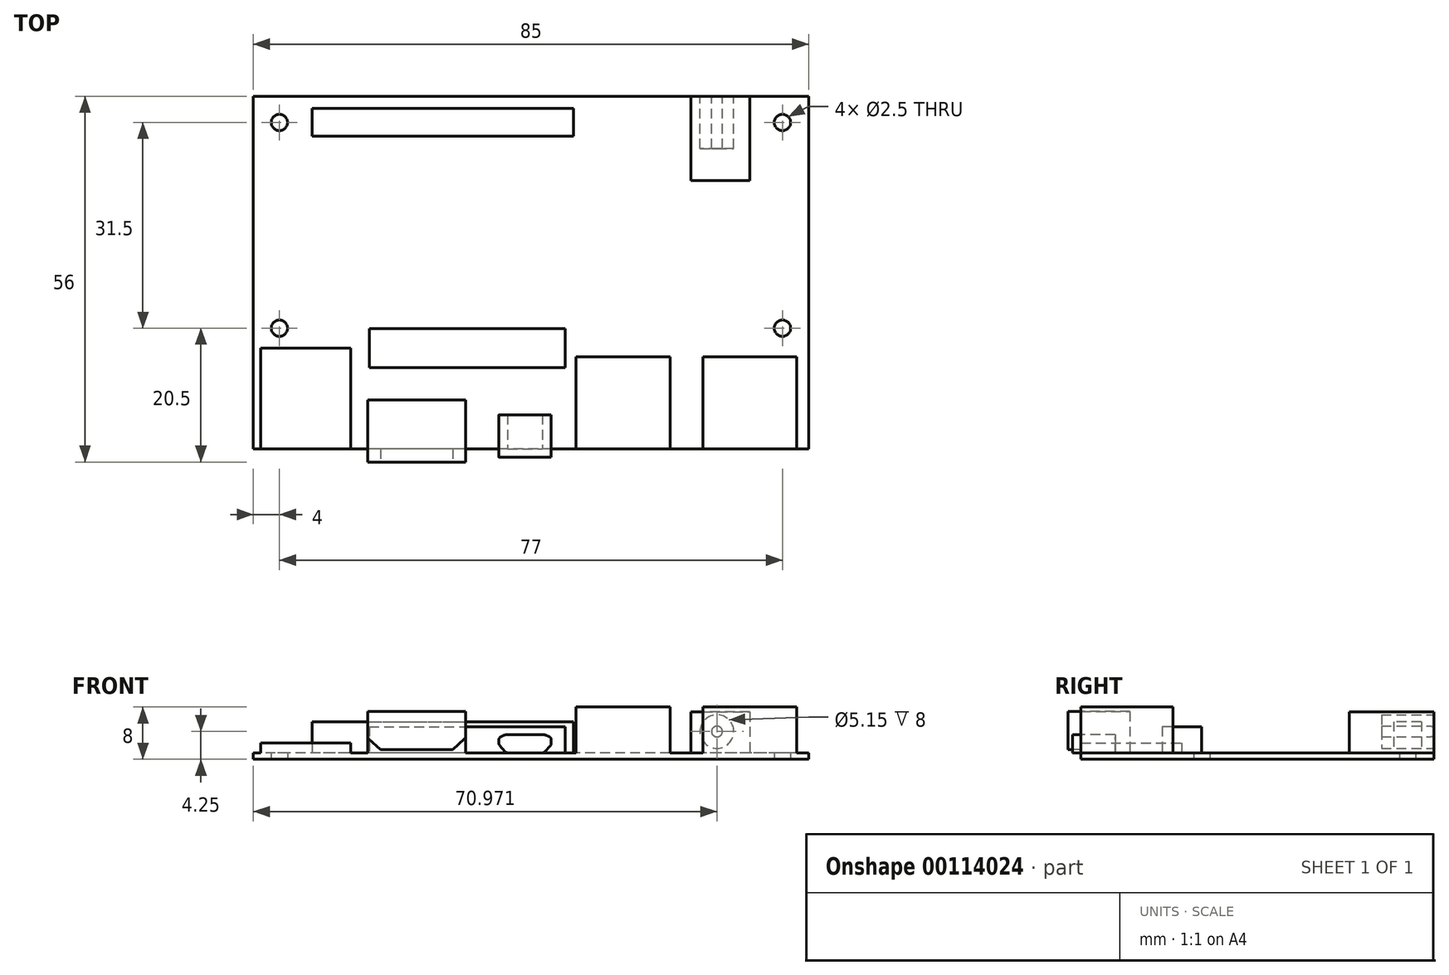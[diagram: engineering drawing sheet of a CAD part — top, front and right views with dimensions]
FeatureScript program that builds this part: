
annotation { "Feature Type Name" : "Feature", "Feature Type Description" : "" }
export const myFeature = defineFeature(function(context is Context, id is Id, definition is map)
    precondition{}
    {
        {
            var Q0;
            Q0=qCreatedBy(makeId("Top.planeOp"),FACE);
            var sketch = newSketch(context, id + "F0", { "sketchPlane" : qUnion([Q0])});
            skLineSegment(sketch, "E0.bottom", {"start": v(42.5, -27) * mm, "end": v(-42.5, -27) * mm});
            skLineSegment(sketch, "E0.top", {"start": v(42.5, 27) * mm, "end": v(-42.5, 27) * mm});
            skLineSegment(sketch, "E0.left", {"start": v(42.5, -27) * mm, "end": v(42.5, 27) * mm});
            skLineSegment(sketch, "E0.right", {"start": v(-42.5, -27) * mm, "end": v(-42.5, 27) * mm});
            skPoint(sketch, "E0.middle", {"position": v(0, 0) * mm});
            skLineSegment(sketch, "E1", {"start": v(-38.5, 27) * mm, "end": v(-38.5, -27) * mm, "construction": true});
            skLineSegment(sketch, "E2", {"start": v(38.5, 27) * mm, "end": v(38.5, -27) * mm, "construction": true});
            skLineSegment(sketch, "E3", {"start": v(-42.5, 23) * mm, "end": v(42.5, 23) * mm, "construction": true});
            skLineSegment(sketch, "E4", {"start": v(-42.5, -8.5) * mm, "end": v(42.5, -8.5) * mm, "construction": true});
            skPoint(sketch, "E5", {"position": v(-38.5, 23) * mm});
            skPoint(sketch, "E6", {"position": v(38.5, 23) * mm});
            skPoint(sketch, "E7", {"position": v(38.5, -8.5) * mm});
            skPoint(sketch, "E8", {"position": v(-38.5, -8.5) * mm});
            skCircle(sketch, "E9", {"center": v(-38.5, 23) * mm, "radius": 1.25 * mm});
            skCircle(sketch, "E10", {"center": v(38.5, 23) * mm, "radius": 1.25 * mm});
            skCircle(sketch, "E11", {"center": v(38.5, -8.5) * mm, "radius": 1.25 * mm});
            skCircle(sketch, "E12", {"center": v(-38.5, -8.5) * mm, "radius": 1.25 * mm});
            skSolve(sketch);
        }
        {
            var Q0;
            Q0=makeQuery(id+"F0.imprint","IMPRINT",FACE,{"disambiguationData":[TD([[makeQuery(id+"F0.imprint","IMPRINT",EDGE,{"derivedFrom":sQuery(id+"F0.wireOp",EDGE,"E0.bottom")}),-1.0]])]});
            var sketch = newSketch(context, id + "F1", { "sketchPlane" : qUnion([Q0])});
            skLineSegment(sketch, "E13.bottom", {"start": v(-35, 26.25) * mm, "end": v(8, 26.25) * mm, "construction": true});
            skLineSegment(sketch, "E13.top", {"start": v(-35, 19.75) * mm, "end": v(8, 19.75) * mm, "construction": true});
            skLineSegment(sketch, "E13.left", {"start": v(-35, 26.25) * mm, "end": v(-35, 19.75) * mm, "construction": true});
            skLineSegment(sketch, "E13.right", {"start": v(8, 26.25) * mm, "end": v(8, 19.75) * mm, "construction": true});
            skPoint(sketch, "E14", {"position": v(-35, 23) * mm});
            skLineSegment(sketch, "E15", {"start": v(-32.5, 26.25) * mm, "end": v(-32.5, 19.75) * mm, "construction": true});
            skPoint(sketch, "E16", {"position": v(-32.53, 23) * mm});
            skLineSegment(sketch, "E17.bottom", {"start": v(-33.5, 25.12) * mm, "end": v(6.5, 25.12) * mm});
            skLineSegment(sketch, "E17.top", {"start": v(-33.5, 20.88) * mm, "end": v(6.5, 20.88) * mm});
            skLineSegment(sketch, "E17.left", {"start": v(-33.5, 25.12) * mm, "end": v(-33.5, 20.87) * mm});
            skLineSegment(sketch, "E17.right", {"start": v(6.5, 25.12) * mm, "end": v(6.5, 20.87) * mm});
            skSolve(sketch);
        }
        {
            var Q0;
            Q0=makeQuery(id+"F0.imprint","IMPRINT",FACE,{"disambiguationData":[TD([[makeQuery(id+"F0.imprint","IMPRINT",EDGE,{"derivedFrom":sQuery(id+"F0.wireOp",EDGE,"E0.bottom")}),-1.0]])]});
            var sketch = newSketch(context, id + "F2", { "sketchPlane" : qUnion([Q0])});
            skLineSegment(sketch, "E18.0", {"start": v(42.5, 27) * mm, "end": v(-42.5, 27) * mm});
            skLineSegment(sketch, "E19", {"start": v(24.5, 27) * mm, "end": v(24.5, 14.1) * mm});
            skLineSegment(sketch, "E20", {"start": v(24.5, 14.1) * mm, "end": v(33.5, 14.1) * mm});
            skLineSegment(sketch, "E21", {"start": v(33.5, 14.1) * mm, "end": v(33.5, 27) * mm});
            skLineSegment(sketch, "E22", {"start": v(29, 14.1) * mm, "end": v(29, 27) * mm, "construction": true});
            skLineSegment(sketch, "E23.0", {"start": v(-42.5, -27) * mm, "end": v(-42.5, 27) * mm});
            skSolve(sketch);
        }
        {
            var Q0;
            Q0=makeQuery(id+"F0.imprint","IMPRINT",FACE,{"disambiguationData":[TD([[makeQuery(id+"F0.imprint","IMPRINT",EDGE,{"derivedFrom":sQuery(id+"F0.wireOp",EDGE,"E0.bottom")}),-1.0]])]});
            var sketch = newSketch(context, id + "F3", { "sketchPlane" : qUnion([Q0])});
            skLineSegment(sketch, "E24.0", {"start": v(-42.5, -27) * mm, "end": v(-42.5, 27) * mm});
            skLineSegment(sketch, "E25.0", {"start": v(42.5, -27) * mm, "end": v(42.5, 27) * mm});
            skLineSegment(sketch, "E26", {"start": v(-42.5, -11.55) * mm, "end": v(42.5, -11.55) * mm, "construction": true});
            skLineSegment(sketch, "E27.0", {"start": v(42.5, -27) * mm, "end": v(-42.5, -27) * mm});
            skLineSegment(sketch, "E28", {"start": v(-34.5, -27) * mm, "end": v(-34.5, -11.55) * mm, "construction": true});
            skLineSegment(sketch, "E29", {"start": v(-17.5, -27) * mm, "end": v(-17.5, -11.55) * mm, "construction": true});
            skLineSegment(sketch, "E30", {"start": v(-25, -27) * mm, "end": v(-25, -19.5) * mm});
            skLineSegment(sketch, "E31", {"start": v(-25, -19.5) * mm, "end": v(-10, -19.5) * mm});
            skLineSegment(sketch, "E32", {"start": v(-10, -19.5) * mm, "end": v(-10, -27) * mm});
            skLineSegment(sketch, "E33", {"start": v(-41.38, -27) * mm, "end": v(-41.39, -11.55) * mm});
            skLineSegment(sketch, "E34", {"start": v(-41.39, -11.55) * mm, "end": v(-27.62, -11.55) * mm});
            skLineSegment(sketch, "E35", {"start": v(-27.62, -11.55) * mm, "end": v(-27.62, -27) * mm});
            skLineSegment(sketch, "E36", {"start": v(-0.9, -11.55) * mm, "end": v(-0.9, -27) * mm, "construction": true});
            skLineSegment(sketch, "E37", {"start": v(-4.9, -27) * mm, "end": v(-4.9, -21.75) * mm});
            skLineSegment(sketch, "E38", {"start": v(-4.9, -21.75) * mm, "end": v(3.1, -21.75) * mm});
            skLineSegment(sketch, "E39", {"start": v(3.1, -21.75) * mm, "end": v(3.1, -27) * mm});
            skLineSegment(sketch, "E40", {"start": v(14.1, -27) * mm, "end": v(14.1, -11.55) * mm, "construction": true});
            skLineSegment(sketch, "E41", {"start": v(33.5, -27) * mm, "end": v(33.5, -11.55) * mm, "construction": true});
            skLineSegment(sketch, "E42", {"start": v(6.9, -27) * mm, "end": v(6.9, -12.9) * mm});
            skLineSegment(sketch, "E43", {"start": v(6.9, -12.9) * mm, "end": v(21.3, -12.9) * mm});
            skLineSegment(sketch, "E44", {"start": v(21.3, -12.9) * mm, "end": v(21.3, -27) * mm});
            skLineSegment(sketch, "E45", {"start": v(26.3, -27) * mm, "end": v(26.3, -12.9) * mm});
            skLineSegment(sketch, "E46", {"start": v(26.3, -12.9) * mm, "end": v(40.7, -12.9) * mm});
            skLineSegment(sketch, "E47", {"start": v(40.7, -12.9) * mm, "end": v(40.7, -27) * mm});
            skLineSegment(sketch, "E48", {"start": v(-25, -27) * mm, "end": v(-25, -29) * mm});
            skLineSegment(sketch, "E49", {"start": v(-25, -29) * mm, "end": v(-10, -29) * mm});
            skLineSegment(sketch, "E50", {"start": v(-10, -29) * mm, "end": v(-10, -27) * mm});
            skLineSegment(sketch, "E51", {"start": v(-4.9, -27) * mm, "end": v(-4.9, -28.25) * mm});
            skLineSegment(sketch, "E52", {"start": v(-4.9, -28.25) * mm, "end": v(3.1, -28.25) * mm});
            skLineSegment(sketch, "E53", {"start": v(3.1, -28.25) * mm, "end": v(3.1, -27) * mm});
            skSolve(sketch);
        }
        {
            var Q0;
            Q0=makeQuery(id+"F0.imprint","IMPRINT",FACE,{"disambiguationData":[TD([[makeQuery(id+"F0.imprint","IMPRINT",EDGE,{"derivedFrom":sQuery(id+"F0.wireOp",EDGE,"E0.bottom")}),-1.0]])]});
            var sketch = newSketch(context, id + "F4", { "sketchPlane" : qUnion([Q0])});
            skLineSegment(sketch, "E54.bottom", {"start": v(-24.76, -8.55) * mm, "end": v(5.24, -8.55) * mm});
            skLineSegment(sketch, "E54.top", {"start": v(-24.76, -14.55) * mm, "end": v(5.24, -14.55) * mm});
            skLineSegment(sketch, "E54.left", {"start": v(-24.76, -8.55) * mm, "end": v(-24.76, -14.55) * mm});
            skLineSegment(sketch, "E54.right", {"start": v(5.24, -8.55) * mm, "end": v(5.24, -14.55) * mm});
            skLineSegment(sketch, "E55.0", {"start": v(-21.35, -27) * mm, "end": v(-21.35, -11.55) * mm});
            skLineSegment(sketch, "E55.1", {"start": v(-42.5, -27) * mm, "end": v(-42.5, 27) * mm});
            skSolve(sketch);
        }
        {
            var Q0;
            Q0=qSketchRegion(id+"F0",true);
            extrude(context, id + "F5", {"entities" : qUnion([Q0]), "depth" : 1 * mm});
        }
        {
            var Q0;
            {var subQ0=sQuery(id+"F3.wireOp",EDGE,"E45");Q0=makeQuery(id+"F3.imprint","IMPRINT",FACE,{"disambiguationData":[TD([[makeQuery(id+"F3.imprint","IMPRINT",EDGE,{"derivedFrom":subQ0}),-1.0]])]});}
            var Q1;
            {var subQ0=sQuery(id+"F3.wireOp",EDGE,"E42");Q1=makeQuery(id+"F3.imprint","IMPRINT",FACE,{"disambiguationData":[TD([[makeQuery(id+"F3.imprint","IMPRINT",EDGE,{"derivedFrom":subQ0}),-1.0]])]});}
            extrude(context, id + "F6", {"entities" : qUnion([Q0, Q1]), "operationType" : NewBodyOperationType.ADD, "depth" : 8 * mm});
        }
        {
            var Q0;
            {var subQ0=sQuery(id+"F3.wireOp",EDGE,"E51");Q0=makeQuery(id+"F3.imprint","IMPRINT",FACE,{"disambiguationData":[TD([[makeQuery(id+"F3.imprint","IMPRINT",EDGE,{"derivedFrom":subQ0}),1.0]])]});}
            var Q1;
            {var subQ0=sQuery(id+"F3.wireOp",EDGE,"E37");Q1=makeQuery(id+"F3.imprint","IMPRINT",FACE,{"disambiguationData":[TD([[makeQuery(id+"F3.imprint","IMPRINT",EDGE,{"derivedFrom":subQ0}),-1.0]])]});}
            extrude(context, id + "F7", {"entities" : qUnion([Q0, Q1]), "operationType" : NewBodyOperationType.ADD, "depth" : 3.75 * mm});
        }
        {
            var Q0;
            {var subQ0=sQuery(id+"F3.wireOp",EDGE,"E48");Q0=makeQuery(id+"F3.imprint","IMPRINT",FACE,{"disambiguationData":[TD([[makeQuery(id+"F3.imprint","IMPRINT",EDGE,{"derivedFrom":subQ0}),1.0]])]});}
            var Q1;
            {var subQ0=sQuery(id+"F3.wireOp",EDGE,"E30");Q1=makeQuery(id+"F3.imprint","IMPRINT",FACE,{"disambiguationData":[TD([[makeQuery(id+"F3.imprint","IMPRINT",EDGE,{"derivedFrom":subQ0}),-1.0]])]});}
            extrude(context, id + "F8", {"entities" : qUnion([Q0, Q1]), "operationType" : NewBodyOperationType.ADD, "depth" : 7.3 * mm});
        }
        {
            var Q0;
            {var subQ0=sQuery(id+"F3.wireOp",EDGE,"E33");Q0=makeQuery(id+"F3.imprint","IMPRINT",FACE,{"disambiguationData":[TD([[makeQuery(id+"F3.imprint","IMPRINT",EDGE,{"derivedFrom":subQ0}),-1.0]])]});}
            extrude(context, id + "F9", {"entities" : qUnion([Q0]), "operationType" : NewBodyOperationType.ADD, "depth" : 2.5 * mm});
        }
        {
            var Q0;
            {var subQ0=sQuery(id+"F2.wireOp",EDGE,"E19");Q0=makeQuery(id+"F2.imprint","IMPRINT",FACE,{"disambiguationData":[TD([[makeQuery(id+"F2.imprint","IMPRINT",EDGE,{"derivedFrom":subQ0}),1.0]])]});}
            extrude(context, id + "F10", {"entities" : qUnion([Q0]), "operationType" : NewBodyOperationType.ADD, "depth" : 7.25 * mm});
        }
        {
            var Q0;
            Q0=qSketchRegion(id+"F1",true);
            extrude(context, id + "F11", {"entities" : qUnion([Q0]), "operationType" : NewBodyOperationType.ADD, "depth" : 5.75 * mm});
        }
        {
            var Q0;
            Q0=qSketchRegion(id+"F4",true);
            extrude(context, id + "F12", {"entities" : qUnion([Q0]), "operationType" : NewBodyOperationType.ADD, "depth" : 5 * mm});
        }
        {
            var Q0;
            Q0=makeQuery(id+"F7.opExtrude","SWEPT_FACE",FACE,{"disambiguationData":[OSD([sQuery(id+"F3.wireOp",EDGE,"E52")])]});
            var sketch = newSketch(context, id + "F13", { "sketchPlane" : qUnion([Q0])});
            skPoint(sketch, "E56", {"position": v(-0.9, 0) * mm});
            skLineSegment(sketch, "E57", {"start": v(-4.9, 0) * mm, "end": v(-0.9, 0) * mm, "construction": true});
            skPoint(sketch, "E58", {"position": v(-2.9, 0) * mm});
            skLineSegment(sketch, "E59", {"start": v(-0.9, 0) * mm, "end": v(3.1, 0) * mm, "construction": true});
            skPoint(sketch, "E60", {"position": v(1.1, 0) * mm});
            skLineSegment(sketch, "E61", {"start": v(-4.77, 2.1) * mm, "end": v(-3.94, 1.17) * mm});
            skLineSegment(sketch, "E62", {"start": v(2.15, 1.17) * mm, "end": v(2.97, 2.08) * mm});
            skPoint(sketch, "E63", {"position": v(-3.94, 3.75) * mm});
            skPoint(sketch, "E64", {"position": v(2.14, 3.75) * mm});
            skLineSegment(sketch, "E65", {"start": v(-0.9, 0) * mm, "end": v(-0.9, 3.75) * mm, "construction": true});
            skLineSegment(sketch, "E66", {"start": v(-4.6, 3.48) * mm, "end": v(-4.08, 3.7) * mm});
            skLineSegment(sketch, "E67", {"start": v(2.8, 3.46) * mm, "end": v(2.28, 3.69) * mm});
            skLineSegment(sketch, "E68", {"start": v(-4.9, 2.24) * mm, "end": v(3.1, 2.22) * mm, "construction": true});
            skLineSegment(sketch, "E69", {"start": v(-4.9, 3.35) * mm, "end": v(3.1, 3.33) * mm, "construction": true});
            skLineSegment(sketch, "E70", {"start": v(-4.9, 3.02) * mm, "end": v(-4.9, 2.43) * mm});
            skLineSegment(sketch, "E71", {"start": v(3.1, 3) * mm, "end": v(3.1, 2.42) * mm});
            skLineSegment(sketch, "E72", {"start": v(-3.8, 3.75) * mm, "end": v(2, 3.75) * mm});
            skLineSegment(sketch, "E73", {"start": v(-2.73, 0) * mm, "end": v(0.87, 0) * mm});
            skPoint(sketch, "E74.visualSharp", {"position": v(3.1, 2.22) * mm});
            skArc(sketch, "E74.filletArc", {"start": v(2.97, 2.08) * mm, "mid": v(3.07, 2.24) * mm, "end": v(3.1, 2.42) * mm});
            skPoint(sketch, "E75.visualSharp", {"position": v(3.1, 3.33) * mm});
            skArc(sketch, "E75.filletArc", {"start": v(3.1, 3) * mm, "mid": v(3.02, 3.28) * mm, "end": v(2.8, 3.46) * mm});
            skArc(sketch, "E76.filletArc", {"start": v(2.28, 3.69) * mm, "mid": v(2.14, 3.73) * mm, "end": v(2, 3.75) * mm});
            skArc(sketch, "E77.filletArc", {"start": v(-3.8, 3.75) * mm, "mid": v(-3.94, 3.74) * mm, "end": v(-4.08, 3.7) * mm});
            skPoint(sketch, "E78.visualSharp", {"position": v(-4.9, 3.35) * mm});
            skArc(sketch, "E78.filletArc", {"start": v(-4.6, 3.48) * mm, "mid": v(-4.82, 3.3) * mm, "end": v(-4.9, 3.02) * mm});
            skPoint(sketch, "E79.visualSharp", {"position": v(-4.9, 2.24) * mm});
            skArc(sketch, "E79.filletArc", {"start": v(-4.9, 2.43) * mm, "mid": v(-4.87, 2.25) * mm, "end": v(-4.77, 2.1) * mm});
            skLineSegment(sketch, "E80.0", {"start": v(24.5, 1) * mm, "end": v(-42.5, 1) * mm});
            skLineSegment(sketch, "E81", {"start": v(-3.57, 1) * mm, "end": v(1.78, 1) * mm});
            skPoint(sketch, "E82.visualSharp", {"position": v(-3.8, 1) * mm});
            skArc(sketch, "E82.filletArc", {"start": v(-3.94, 1.17) * mm, "mid": v(-3.77, 1.04) * mm, "end": v(-3.57, 1) * mm});
            skPoint(sketch, "E83.visualSharp", {"position": v(2, 1) * mm});
            skArc(sketch, "E83.filletArc", {"start": v(1.78, 1) * mm, "mid": v(1.98, 1.04) * mm, "end": v(2.15, 1.17) * mm});
            skSolve(sketch);
        }
        {
            var Q0;
            Q0=makeQuery(id+"F13.imprint","IMPRINT",FACE,{"disambiguationData":[TD([[makeQuery(id+"F13.imprint","IMPRINT",EDGE,{"derivedFrom":sQuery(id+"F13.wireOp",EDGE,"E61")}),-1.0]])]});
            var Q1;
            Q1=makeQuery(id+"F13.imprint","IMPRINT",FACE,{"disambiguationData":[TD([[makeQuery(id+"F13.imprint","IMPRINT",EDGE,{"derivedFrom":sQuery(id+"F13.wireOp",EDGE,"E66")}),1.0]])]});
            var Q2;
            Q2=makeQuery(id+"F13.imprint","IMPRINT",FACE,{"disambiguationData":[TD([[makeQuery(id+"F13.imprint","IMPRINT",EDGE,{"derivedFrom":sQuery(id+"F13.wireOp",EDGE,"E67")}),-1.0]])]});
            var Q3;
            Q3=makeQuery(id+"F13.imprint","IMPRINT",FACE,{"disambiguationData":[TD([[makeQuery(id+"F13.imprint","IMPRINT",EDGE,{"derivedFrom":sQuery(id+"F13.wireOp",EDGE,"E62")}),-1.0]])]});
            var Q4;
            {var subQ8=sQuery(id+"F13.wireOp",EDGE,"a18c98a6-a4a7-4cf6-845e-3db316127b87.filletArc");Q4=makeQuery(id+"F13.imprint","IMPRINT",FACE,{"disambiguationData":[TD([[makeQuery(id+"F13.imprint","IMPRINT",EDGE,{"derivedFrom":subQ8}),-1.0]])]});}
            var Q5;
            {var subQ6=sQuery(id+"F13.wireOp",EDGE,"c999dc16-cddd-47d2-9ace-dcb4409ff7b4.filletArc");Q5=makeQuery(id+"F13.imprint","IMPRINT",FACE,{"disambiguationData":[TD([[makeQuery(id+"F13.imprint","IMPRINT",EDGE,{"derivedFrom":subQ6}),-1.0]])]});}
            var Q6;
            {var subQ9=sQuery(id+"F13.wireOp",EDGE,"E73");Q6=makeQuery(id+"F13.imprint","IMPRINT",FACE,{"disambiguationData":[TD([[makeQuery(id+"F13.imprint","IMPRINT",EDGE,{"derivedFrom":subQ9}),1.0]])]});}
            var Q7;
            {var subQ0=sQuery(id+"F3.wireOp",EDGE,"E51");var subQ1=sQuery(id+"F3.wireOp",EDGE,"E37");var subQ2=makeQuery(id+"F7.opExtrude","SWEPT_FACE",FACE,{"disambiguationData":[OSD([subQ1,subQ0])]});var subQ8=sQuery(id+"F0.wireOp",EDGE,"E0.right");var subQ11=sQuery(id+"F0.wireOp",EDGE,"E0.bottom");var subQ16=sQuery(id+"F3.wireOp",EDGE,"E27.0");Q7=makeQuery(id+"F8.boolean.opBoolean","SPLIT",FACE,{"disambiguationData":[TD([subQ2])],"derivedFrom":makeQuery(id+"F7.boolean.opBoolean","SPLIT",FACE,{"disambiguationData":[TD([makeQuery(id+"F5.opExtrude","SWEPT_FACE",FACE,{"disambiguationData":[OSD([subQ8])]})])],"derivedFrom":makeQuery(id+"F6.boolean.opBoolean","MERGE",FACE,{"derivedFrom":[makeQuery(id+"F5.opExtrude","SWEPT_FACE",FACE,{"disambiguationData":[OSD([subQ11])]}),makeQuery(id+"F6.opExtrude","SWEPT_FACE",FACE,{"disambiguationData":[OSD([subQ16]),TDD([makeQuery(id+"F3.imprint","IMPRINT",EDGE,{"disambiguationData":[TD([[makeQuery(id+"F3.imprint","INTERSECT",VERTEX,{"derivedFrom":[subQ16,sQuery(id+"F3.wireOp",EDGE,"E45")]}),1.0]])],"derivedFrom":subQ16})])]}),makeQuery(id+"F6.opExtrude","SWEPT_FACE",FACE,{"disambiguationData":[OSD([subQ16]),TDD([makeQuery(id+"F3.imprint","IMPRINT",EDGE,{"disambiguationData":[TD([[makeQuery(id+"F3.imprint","INTERSECT",VERTEX,{"derivedFrom":[subQ16,sQuery(id+"F3.wireOp",EDGE,"E42")]}),1.0]])],"derivedFrom":subQ16})])]})]})})});}
            extrude(context, id + "F14", {"entities" : qUnion([Q0, Q1, Q2, Q3, Q4, Q5, Q6]), "operationType" : NewBodyOperationType.REMOVE, "endBound" : BoundingType.UP_TO_SURFACE, "oppositeDirection" : true, "endBoundEntityFace" : qUnion([Q7]), "depth" : 25 * mm});
        }
        {
            var Q0;
            Q0=makeQuery(id+"F14.boolean.opBoolean","COPY",FACE,{"derivedFrom":makeQuery(id+"F14.opExtrude","CAP_FACE",FACE,{"disambiguationData":[OSD([sQuery(id+"F3.wireOp",EDGE,"E51"),sQuery(id+"F3.wireOp",EDGE,"E52"),sQuery(id+"F13.wireOp",EDGE,"E66"),sQuery(id+"F13.wireOp",EDGE,"E77.filletArc"),sQuery(id+"F13.wireOp",EDGE,"E78.filletArc")])],"isStart":false})});
            var Q1;
            Q1=makeQuery(id+"F14.boolean.opBoolean","COPY",FACE,{"derivedFrom":makeQuery(id+"F14.opExtrude","CAP_FACE",FACE,{"disambiguationData":[OSD([sQuery(id+"F3.wireOp",EDGE,"E52"),sQuery(id+"F3.wireOp",EDGE,"E53"),sQuery(id+"F13.wireOp",EDGE,"E67"),sQuery(id+"F13.wireOp",EDGE,"E75.filletArc"),sQuery(id+"F13.wireOp",EDGE,"E76.filletArc")])],"isStart":false})});
            var Q2;
            {var subQ0=sQuery(id+"F13.wireOp",EDGE,"E79.filletArc");Q2=makeQuery(id+"F13.imprint","IMPRINT",FACE,{"disambiguationData":[TD([[makeQuery(id+"F13.imprint","IMPRINT",EDGE,{"derivedFrom":subQ0}),-1.0]])]});}
            var Q3;
            {var subQ0=sQuery(id+"F13.wireOp",EDGE,"E74.filletArc");Q3=makeQuery(id+"F13.imprint","IMPRINT",FACE,{"disambiguationData":[TD([[makeQuery(id+"F13.imprint","IMPRINT",EDGE,{"derivedFrom":subQ0}),-1.0]])]});}
            var Q4;
            Q4=makeQuery(id+"F7.opExtrude","SWEPT_FACE",FACE,{"disambiguationData":[OSD([sQuery(id+"F3.wireOp",EDGE,"E38")])]});
            extrude(context, id + "F15", {"entities" : qUnion([Q0, Q1, Q2, Q3]), "operationType" : NewBodyOperationType.REMOVE, "endBound" : BoundingType.UP_TO_SURFACE, "oppositeDirection" : true, "endBoundEntityFace" : qUnion([Q4]), "depth" : 25 * mm});
        }
        {
            var Q0;
            Q0=makeQuery(id+"F8.opExtrude","SWEPT_FACE",FACE,{"disambiguationData":[OSD([sQuery(id+"F3.wireOp",EDGE,"E49")])]});
            var sketch = newSketch(context, id + "F16", { "sketchPlane" : qUnion([Q0])});
            skLineSegment(sketch, "E84.0", {"start": v(-25, 7.3) * mm, "end": v(-10, 7.3) * mm});
            skLineSegment(sketch, "E85.0", {"start": v(-10, 7.3) * mm, "end": v(-10, 3.52) * mm});
            skLineSegment(sketch, "E86.0", {"start": v(-25, 7.3) * mm, "end": v(-25, 3.52) * mm});
            skLineSegment(sketch, "E87.0", {"start": v(24.5, 1) * mm, "end": v(-10, 1) * mm});
            skLineSegment(sketch, "E88.0", {"start": v(-25, 0) * mm, "end": v(-10, 0) * mm});
            skLineSegment(sketch, "E89", {"start": v(-17.5, 7.3) * mm, "end": v(-17.5, 1) * mm, "construction": true});
            skPoint(sketch, "E90", {"position": v(-13.16, 1) * mm});
            skPoint(sketch, "E91", {"position": v(-21.84, 1) * mm});
            skLineSegment(sketch, "E92", {"start": v(-24.84, 3.15) * mm, "end": v(-23.04, 1.5) * mm});
            skLineSegment(sketch, "E93", {"start": v(-11.96, 1.5) * mm, "end": v(-10.16, 3.15) * mm});
            skLineSegment(sketch, "E94.trimOffspring", {"start": v(-10, 1) * mm, "end": v(-10, 0) * mm});
            skLineSegment(sketch, "E95.trimOffspring", {"start": v(-25, 1) * mm, "end": v(-25, 0) * mm});
            skPoint(sketch, "E96.visualSharp", {"position": v(-25, 3.3) * mm});
            skArc(sketch, "E96.filletArc", {"start": v(-25, 3.52) * mm, "mid": v(-24.96, 3.32) * mm, "end": v(-24.84, 3.15) * mm});
            skPoint(sketch, "E97.visualSharp", {"position": v(-10, 3.3) * mm});
            skArc(sketch, "E97.filletArc", {"start": v(-10.16, 3.15) * mm, "mid": v(-10.04, 3.32) * mm, "end": v(-10, 3.52) * mm});
            skLineSegment(sketch, "E98", {"start": v(-25, 1.5) * mm, "end": v(-23.04, 1.5) * mm, "construction": true});
            skPoint(sketch, "E99", {"position": v(-23.04, 1.5) * mm});
            skPoint(sketch, "E100", {"position": v(-11.96, 1.5) * mm});
            skLineSegment(sketch, "E101.trimOffspring", {"start": v(-11.96, 1.5) * mm, "end": v(-10, 1.5) * mm, "construction": true});
            skLineSegment(sketch, "E102", {"start": v(-23.04, 1.5) * mm, "end": v(-11.96, 1.5) * mm});
            skLineSegment(sketch, "E103.trimOffspring", {"start": v(-25, 1) * mm, "end": v(-42.5, 1) * mm});
            skSolve(sketch);
        }
        {
            var Q0;
            {var subQ0=sQuery(id+"F16.wireOp",EDGE,"E92");Q0=makeQuery(id+"F16.imprint","IMPRINT",FACE,{"disambiguationData":[TD([[makeQuery(id+"F16.imprint","IMPRINT",EDGE,{"derivedFrom":subQ0}),-1.0]])]});}
            var Q1;
            {var subQ0=sQuery(id+"F16.wireOp",EDGE,"E93");Q1=makeQuery(id+"F16.imprint","IMPRINT",FACE,{"disambiguationData":[TD([[makeQuery(id+"F16.imprint","IMPRINT",EDGE,{"derivedFrom":subQ0}),-1.0]])]});}
            var Q2;
            {var subQ3=sQuery(id+"F16.wireOp",EDGE,"E88.0");Q2=makeQuery(id+"F16.imprint","IMPRINT",FACE,{"disambiguationData":[TD([[makeQuery(id+"F16.imprint","IMPRINT",EDGE,{"derivedFrom":subQ3}),1.0]])]});}
            var Q3;
            {var subQ0=sQuery(id+"F3.wireOp",EDGE,"E53");var subQ1=sQuery(id+"F3.wireOp",EDGE,"E52");var subQ2=sQuery(id+"F3.wireOp",EDGE,"E51");var subQ3=sQuery(id+"F3.wireOp",EDGE,"E37");var subQ4=makeQuery(id+"F7.opExtrude","SWEPT_FACE",FACE,{"disambiguationData":[OSD([subQ3,subQ2])]});var subQ11=sQuery(id+"F0.wireOp",EDGE,"E0.right");var subQ12=sQuery(id+"F0.wireOp",EDGE,"E0.left");var subQ14=sQuery(id+"F0.wireOp",EDGE,"E0.bottom");var subQ19=sQuery(id+"F3.wireOp",EDGE,"E42");var subQ20=sQuery(id+"F3.wireOp",EDGE,"E27.0");var subQ22=sQuery(id+"F3.wireOp",EDGE,"E45");var subQ24=makeQuery(id+"F6.boolean.opBoolean","MERGE",FACE,{"derivedFrom":[makeQuery(id+"F5.opExtrude","SWEPT_FACE",FACE,{"disambiguationData":[OSD([subQ14])]}),makeQuery(id+"F6.opExtrude","SWEPT_FACE",FACE,{"disambiguationData":[OSD([subQ20]),TDD([makeQuery(id+"F3.imprint","IMPRINT",EDGE,{"disambiguationData":[TD([[makeQuery(id+"F3.imprint","INTERSECT",VERTEX,{"derivedFrom":[subQ20,subQ22]}),1.0]])],"derivedFrom":subQ20})])]}),makeQuery(id+"F6.opExtrude","SWEPT_FACE",FACE,{"disambiguationData":[OSD([subQ20]),TDD([makeQuery(id+"F3.imprint","IMPRINT",EDGE,{"disambiguationData":[TD([[makeQuery(id+"F3.imprint","INTERSECT",VERTEX,{"derivedFrom":[subQ20,subQ19]}),1.0]])],"derivedFrom":subQ20})])]})]});Q3=makeQuery(id+"F14.boolean.opBoolean","MERGE",FACE,{"derivedFrom":[makeQuery(id+"F7.boolean.opBoolean","SPLIT",FACE,{"disambiguationData":[TD([makeQuery(id+"F5.opExtrude","SWEPT_FACE",FACE,{"disambiguationData":[OSD([subQ12])]})])],"derivedFrom":subQ24}),makeQuery(id+"F8.boolean.opBoolean","SPLIT",FACE,{"disambiguationData":[TD([subQ4])],"derivedFrom":makeQuery(id+"F7.boolean.opBoolean","SPLIT",FACE,{"disambiguationData":[TD([makeQuery(id+"F5.opExtrude","SWEPT_FACE",FACE,{"disambiguationData":[OSD([subQ11])]})])],"derivedFrom":subQ24})}),makeQuery(id+"F14.opExtrude","CAP_FACE",FACE,{"disambiguationData":[OSD([subQ2,subQ1,subQ0,sQuery(id+"F13.wireOp",EDGE,"E61"),sQuery(id+"F13.wireOp",EDGE,"E62"),sQuery(id+"F13.wireOp",EDGE,"E73"),sQuery(id+"F13.wireOp",EDGE,"E74.filletArc"),sQuery(id+"F13.wireOp",EDGE,"E79.filletArc"),sQuery(id+"F13.wireOp",EDGE,"E81"),sQuery(id+"F13.wireOp",EDGE,"E82.filletArc"),sQuery(id+"F13.wireOp",EDGE,"E83.filletArc")])],"isStart":false})]});}
            extrude(context, id + "F17", {"entities" : qUnion([Q0, Q1, Q2]), "operationType" : NewBodyOperationType.REMOVE, "endBound" : BoundingType.UP_TO_SURFACE, "oppositeDirection" : true, "endBoundEntityFace" : qUnion([Q3]), "depth" : 25 * mm});
        }
        {
            var Q0;
            Q0=makeQuery(id+"F10.boolean.opBoolean","MERGE",FACE,{"derivedFrom":[makeQuery(id+"F5.opExtrude","SWEPT_FACE",FACE,{"disambiguationData":[OSD([sQuery(id+"F0.wireOp",EDGE,"E0.top")])]}),makeQuery(id+"F10.opExtrude","SWEPT_FACE",FACE,{"disambiguationData":[OSD([sQuery(id+"F2.wireOp",EDGE,"E18.0")])]})]});
            var sketch = newSketch(context, id + "F18", { "sketchPlane" : qUnion([Q0])});
            skLineSegment(sketch, "E104", {"start": v(-28.5, 7.25) * mm, "end": v(-28.5, 1) * mm, "construction": true});
            skCircle(sketch, "E105", {"center": v(-28.47, 4.25) * mm, "radius": 2.58 * mm});
            skCircle(sketch, "E106", {"center": v(-28.47, 4.25) * mm, "radius": 0.82 * mm});
            skLineSegment(sketch, "E107", {"start": v(-33.5, 7.25) * mm, "end": v(-24.5, 7.25) * mm});
            skSolve(sketch);
        }
        {
            var Q0;
            Q0=makeQuery(id+"F18.imprint","IMPRINT",FACE,{"disambiguationData":[TD([[makeQuery(id+"F18.imprint","IMPRINT",EDGE,{"derivedFrom":sQuery(id+"F18.wireOp",EDGE,"E105")}),1.0]])]});
            extrude(context, id + "F19", {"entities" : qUnion([Q0]), "operationType" : NewBodyOperationType.REMOVE, "oppositeDirection" : true, "depth" : 8 * mm});
        }
        {
            var Q0;
            Q0=makeQuery(id+"F19.boolean.opBoolean","SPLIT",FACE,{"disambiguationData":[TD([makeQuery(id+"F19.opExtrude","SWEPT_FACE",FACE,{"disambiguationData":[OSD([sQuery(id+"F18.wireOp",EDGE,"E106")])]})])],"derivedFrom":makeQuery(id+"F10.boolean.opBoolean","MERGE",FACE,{"derivedFrom":[makeQuery(id+"F5.opExtrude","SWEPT_FACE",FACE,{"disambiguationData":[OSD([sQuery(id+"F0.wireOp",EDGE,"E0.top")])]}),makeQuery(id+"F10.opExtrude","SWEPT_FACE",FACE,{"disambiguationData":[OSD([sQuery(id+"F2.wireOp",EDGE,"E18.0")])]})]})});
            fillet(context, id + "F20", {"entities" : qUnion([Q0]), "radius" : 0.4 * mm, "tangentPropagation" : true, "allowEdgeOverflow" : false});
        }
    });
